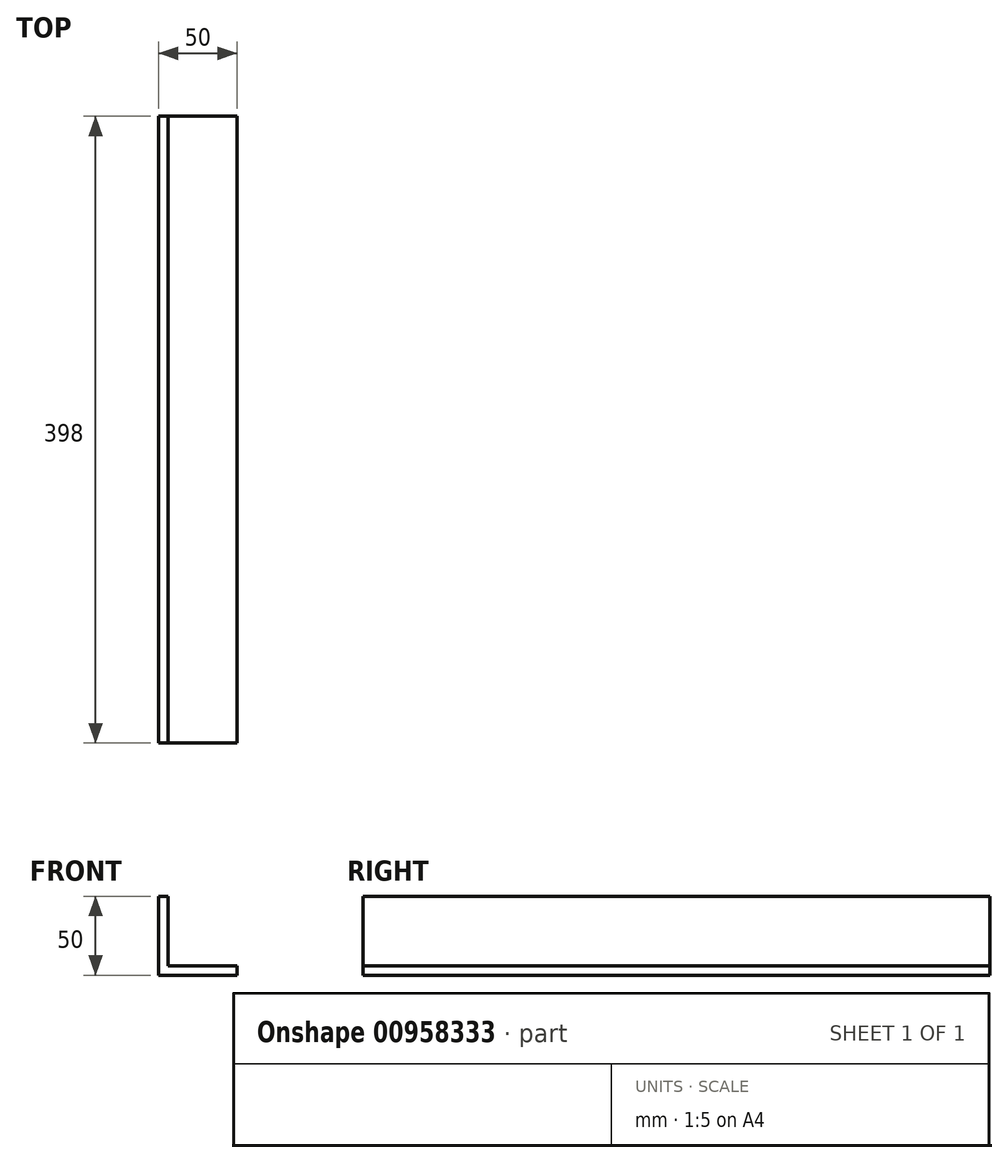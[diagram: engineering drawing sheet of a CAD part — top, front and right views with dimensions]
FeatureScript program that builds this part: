
annotation { "Feature Type Name" : "Feature", "Feature Type Description" : "" }
export const myFeature = defineFeature(function(context is Context, id is Id, definition is map)
    precondition{}
    {
        {
            var Q0;
            Q0=qCreatedBy(makeId("Front.planeOp"),FACE);
            var sketch = newSketch(context, id + "F0", { "sketchPlane" : qUnion([Q0])});
            skLineSegment(sketch, "E0", {"start": v(0, 0) * mm, "end": v(0, 50) * mm});
            skLineSegment(sketch, "E1", {"start": v(0, 50) * mm, "end": v(6, 50) * mm});
            skLineSegment(sketch, "E2", {"start": v(6, 50) * mm, "end": v(6, 6) * mm});
            skLineSegment(sketch, "E3", {"start": v(6, 6) * mm, "end": v(50, 6) * mm});
            skLineSegment(sketch, "E4", {"start": v(50, 6) * mm, "end": v(50, 0) * mm});
            skLineSegment(sketch, "E5", {"start": v(50, 0) * mm, "end": v(0, 0) * mm});
            skSolve(sketch);
        }
        {
            var Q0;
            Q0 = qSketchRegion(id + "F0", true);
            extrude(context, id + "F1", {"entities" : qUnion([Q0]), "depth" : 398 * mm, "offsetDistance" : 25 * mm});
        }
    });
